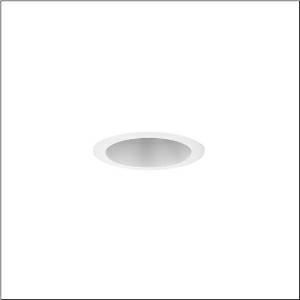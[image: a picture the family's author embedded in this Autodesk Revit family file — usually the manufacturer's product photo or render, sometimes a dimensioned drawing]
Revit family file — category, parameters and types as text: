
# Revit family: lunis_31_mini_51dn15de41
name_source: partatom
category: Lighting Fixtures
units: mm (PartAtom-declared; Revit-internal decimal feet)

## family parameters
Cut with Voids When Loaded = No
Host = Face
Light Source = No
Part Type = Normal
Room Calculation Point = No
Round Connector Dimension = Use Diameter
Shared = No

## types (1)
- Lunis 31 mini (1 x LED, 1040 lm, 8.3 W, 4000K)
    Apparent Load = 8 VA
    CIE Flux Codes = 93 98 100 100 100
    Color Rendering = 80
    Color Temperature = 4000K
    Default Elevation = 1800 mm
    Description = Lunis 31,  mini, downlight, light control with reflector, light emission: direct distribution, LED rated luminous flux: 1.040lm, light colour: 840, control gear: ECG DALI, mains connection: 220..240V, AC, 50/60Hz, housing, white, protection rating (complete): IP20, insulation class (complete): insulation class II (safety insulation), certification: CE, packaging unit: 1 piece
    Height = 0 mm  [stored 0 ft]
    Lamp = 1 x LED
    Lamp Light Flux = 1040 lm
    Lamp Power = 8.3 W
    Lamp count = 1
    Length = 188 mm  [stored 0.616798 ft]
    Luminous efficacy = 125 lm/W
    Manufacturer = Siteco
    ModVariant = No
    Model = 51DN15DE41
    Mounting Place = Ceiling
    Mounting Type = Recessed
    Number of Poles = 1
    OnlyDefault = Yes
    Power Factor = 1
    Product Name = Lunis 31 mini
    Product group = downlight | ceiling recessed
    ProductGroupID = 402
    Protection Class = Protection class II
    Protection Degree = IP 20
    RLX_Detail_Level = 1
    RlxData = <blob elided: 21917 chars, md5=522c4940>
    Socket = socket
    Standby Power = 0 W
    System Light Flux = 1040 lm
    System Power = 8 W
    Type Comments = Product without accessories
    Type Image = l_1005624.jpg
    URL = http://relux.com
    VarID = ---
    Voltage = 0 V
    Weight = 0.00 kg
    Width = 0 mm  [stored 0 ft]

note: [stored X ft] marks values corroborated as IEEE doubles in the binary element streams (Revit-internal decimal feet)

## geometry (parser evidence)
native form markers: Blend x4, Sweep x11
no freeform markers — native parametric forms only
